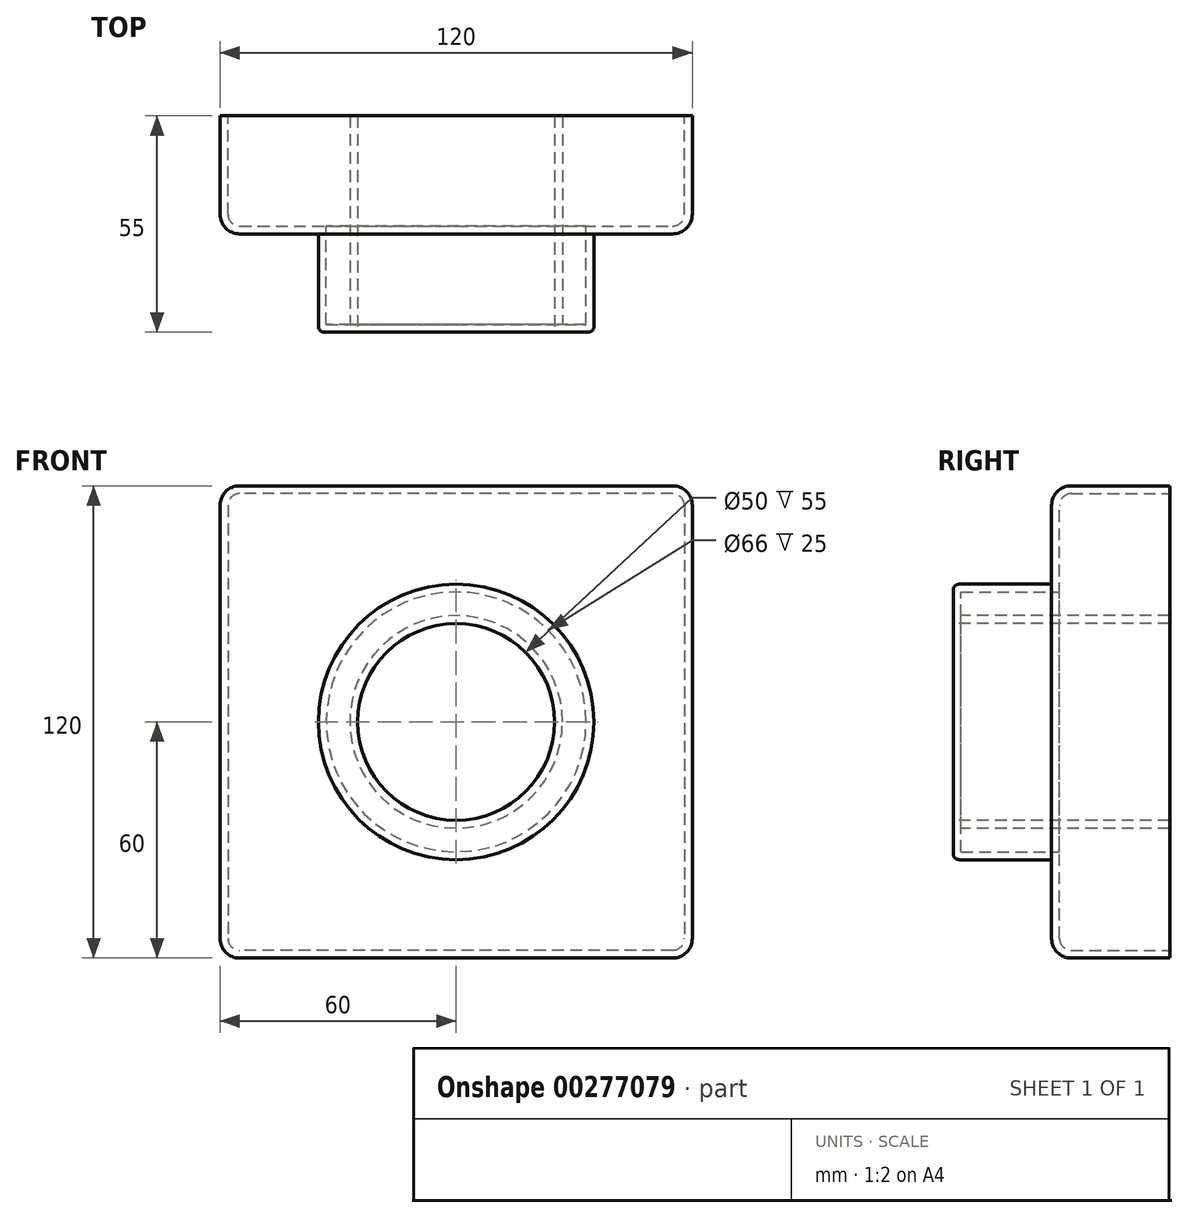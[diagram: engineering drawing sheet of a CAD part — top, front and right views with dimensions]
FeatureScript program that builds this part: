
annotation { "Feature Type Name" : "Feature", "Feature Type Description" : "" }
export const myFeature = defineFeature(function(context is Context, id is Id, definition is map)
    precondition{}
    {
        {
            var Q0;
            Q0=qCreatedBy(makeId("Front.planeOp"),FACE);
            var sketch = newSketch(context, id + "F0", { "sketchPlane" : qUnion([Q0])});
            skLineSegment(sketch, "E0.bottom", {"start": v(60, 60) * mm, "end": v(-60, 60) * mm});
            skLineSegment(sketch, "E0.top", {"start": v(60, -60) * mm, "end": v(-60, -60) * mm});
            skLineSegment(sketch, "E0.left", {"start": v(60, 60) * mm, "end": v(60, -60) * mm});
            skLineSegment(sketch, "E0.right", {"start": v(-60, 60) * mm, "end": v(-60, -60) * mm});
            skPoint(sketch, "E0.middle", {"position": v(0, 0) * mm});
            skSolve(sketch);
        }
        {
            var Q0;
            Q0=qSketchRegion(id+"F0",true);
            extrude(context, id + "F1", {"entities" : qUnion([Q0]), "depth" : 30 * mm});
        }
        {
            var Q0;
            Q0=makeQuery(id+"F1.opExtrude","CAP_FACE",FACE,{"disambiguationData":[OSD([sQuery(id+"F0.wireOp",EDGE,"E0.bottom"),sQuery(id+"F0.wireOp",EDGE,"E0.top"),sQuery(id+"F0.wireOp",EDGE,"E0.left"),sQuery(id+"F0.wireOp",EDGE,"E0.right")])],"isStart":false});
            var sketch = newSketch(context, id + "F2", { "sketchPlane" : qUnion([Q0])});
            skCircle(sketch, "E1", {"center": v(0, 0) * mm, "radius": 35 * mm});
            skSolve(sketch);
        }
        {
            var Q0;
            Q0=makeQuery(id+"F2.imprint","IMPRINT",FACE,{"disambiguationData":[TD([[makeQuery(id+"F2.imprint","IMPRINT",EDGE,{"derivedFrom":sQuery(id+"F2.wireOp",EDGE,"E1")}),1.0]])]});
            extrude(context, id + "F3", {"entities" : qUnion([Q0]), "operationType" : NewBodyOperationType.ADD, "depth" : 25 * mm});
        }
        {
            var Q0;
            Q0=makeQuery(id+"F3.opExtrude","CAP_FACE",FACE,{"disambiguationData":[OSD([sQuery(id+"F2.wireOp",EDGE,"E1")])],"isStart":false});
            var sketch = newSketch(context, id + "F4", { "sketchPlane" : qUnion([Q0])});
            skCircle(sketch, "E2", {"center": v(0, 0) * mm, "radius": 25 * mm});
            skSolve(sketch);
        }
        {
            var Q0;
            Q0=qSketchRegion(id+"F4",true);
            extrude(context, id + "F5", {"entities" : qUnion([Q0]), "operationType" : NewBodyOperationType.REMOVE, "endBound" : BoundingType.THROUGH_ALL, "oppositeDirection" : true, "depth" : 25 * mm});
        }
        {
            var Q0;
            Q0=makeQuery(id+"F3.opExtrude","CAP_EDGE",EDGE,{"disambiguationData":[OSD([sQuery(id+"F2.wireOp",EDGE,"E1")])],"isStart":true});
            var Q1;
            Q1=makeQuery(id+"F1.opExtrude","CAP_EDGE",EDGE,{"disambiguationData":[OSD([sQuery(id+"F0.wireOp",EDGE,"E0.bottom")])],"isStart":false});
            var Q2;
            Q2=makeQuery(id+"F1.opExtrude","CAP_EDGE",EDGE,{"disambiguationData":[OSD([sQuery(id+"F0.wireOp",EDGE,"E0.left")])],"isStart":false});
            var Q3;
            Q3=makeQuery(id+"F1.opExtrude","SWEPT_EDGE",EDGE,{"disambiguationData":[OSD([sQuery(id+"F0.wireOp",EDGE,"E0.bottom"),sQuery(id+"F0.wireOp",EDGE,"E0.left")])]});
            var Q4;
            Q4=makeQuery(id+"F1.opExtrude","SWEPT_EDGE",EDGE,{"disambiguationData":[OSD([sQuery(id+"F0.wireOp",EDGE,"E0.top"),sQuery(id+"F0.wireOp",EDGE,"E0.left")])]});
            var Q5;
            Q5=makeQuery(id+"F1.opExtrude","CAP_EDGE",EDGE,{"disambiguationData":[OSD([sQuery(id+"F0.wireOp",EDGE,"E0.top")])],"isStart":false});
            var Q6;
            Q6=makeQuery(id+"F1.opExtrude","SWEPT_EDGE",EDGE,{"disambiguationData":[OSD([sQuery(id+"F0.wireOp",EDGE,"E0.top"),sQuery(id+"F0.wireOp",EDGE,"E0.right")])]});
            var Q7;
            Q7=makeQuery(id+"F1.opExtrude","CAP_EDGE",EDGE,{"disambiguationData":[OSD([sQuery(id+"F0.wireOp",EDGE,"E0.right")])],"isStart":false});
            var Q8;
            Q8=makeQuery(id+"F1.opExtrude","SWEPT_EDGE",EDGE,{"disambiguationData":[OSD([sQuery(id+"F0.wireOp",EDGE,"E0.bottom"),sQuery(id+"F0.wireOp",EDGE,"E0.right")])]});
            fillet(context, id + "F6", {"entities" : qUnion([Q0, Q1, Q2, Q3, Q4, Q5, Q6, Q7, Q8]), "radius" : 5 * mm, "tangentPropagation" : true, "allowEdgeOverflow" : false});
        }
        {
            var Q0;
            Q0=makeQuery(id+"F3.opExtrude","CAP_EDGE",EDGE,{"disambiguationData":[OSD([sQuery(id+"F2.wireOp",EDGE,"E1")])],"isStart":false});
            fillet(context, id + "F7", {"entities" : qUnion([Q0]), "radius" : 1.5 * mm, "tangentPropagation" : true, "allowEdgeOverflow" : false});
        }
        {
            var Q0;
            Q0=makeQuery(id+"F1.opExtrude","CAP_FACE",FACE,{"disambiguationData":[OSD([sQuery(id+"F0.wireOp",EDGE,"E0.bottom"),sQuery(id+"F0.wireOp",EDGE,"E0.top"),sQuery(id+"F0.wireOp",EDGE,"E0.left"),sQuery(id+"F0.wireOp",EDGE,"E0.right")])],"isStart":true});
            shell(context, id + "F8", {"entities" : qUnion([Q0]), "thickness" : 2 * mm});
        }
    });
